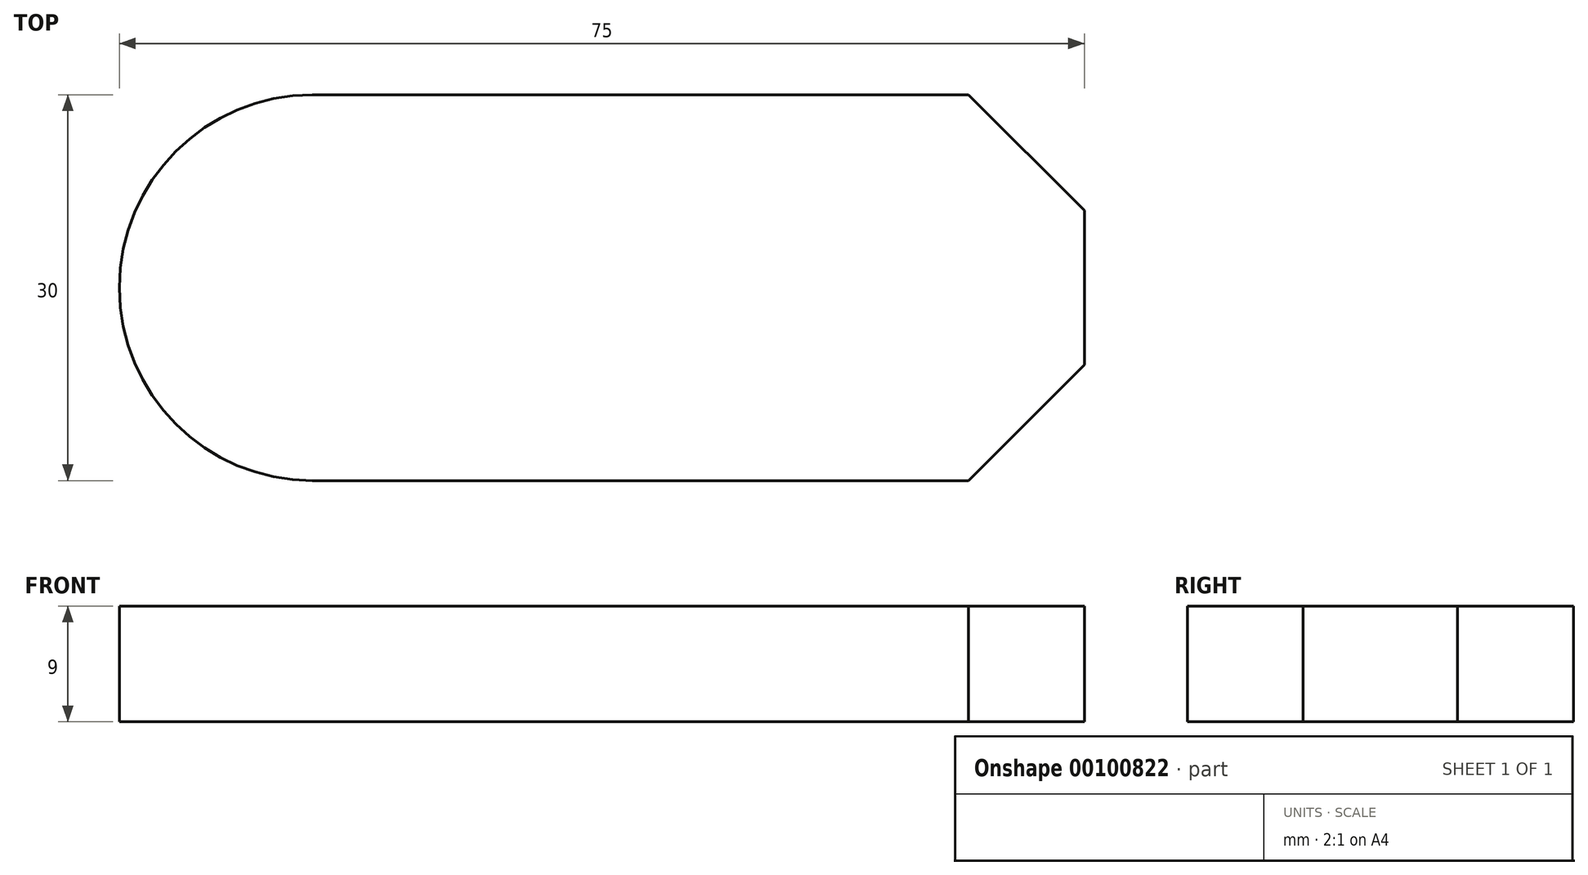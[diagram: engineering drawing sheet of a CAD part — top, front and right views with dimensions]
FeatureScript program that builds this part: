
annotation { "Feature Type Name" : "Feature", "Feature Type Description" : "" }
export const myFeature = defineFeature(function(context is Context, id is Id, definition is map)
    precondition{}
    {
        {
            var Q0;
            Q0=qCreatedBy(makeId("Top.planeOp"),FACE);
            var sketch = newSketch(context, id + "F0", { "sketchPlane" : qUnion([Q0])});
            skLineSegment(sketch, "E0.top", {"start": v(0, 30) * mm, "end": v(51, 30) * mm});
            skArc(sketch, "E1", {"start": v(0, 30) * mm, "mid": v(-15, 15) * mm, "end": v(0, 0) * mm});
            skPoint(sketch, "E2.end.orphan", {"position": v(42.52, 49.43) * mm});
            skPoint(sketch, "E3.end.orphan", {"position": v(42.52, 0) * mm});
            skPoint(sketch, "E4.start.orphan", {"position": v(42.52, 19.13) * mm});
            skLineSegment(sketch, "E5", {"start": v(51, 0) * mm, "end": v(0, 0) * mm});
            skLineSegment(sketch, "E6", {"start": v(60, 21) * mm, "end": v(60, 9) * mm});
            skLineSegment(sketch, "E7", {"start": v(51, 0) * mm, "end": v(60, 9) * mm});
            skLineSegment(sketch, "E8", {"start": v(51, 30) * mm, "end": v(60, 21) * mm});
            skPoint(sketch, "E9.orphan", {"position": v(60, 30) * mm});
            skPoint(sketch, "E10.start.orphan", {"position": v(60, 0) * mm});
            skSolve(sketch);
        }
        {
            var Q0;
            Q0 = qSketchRegion(id + "F0", true);
            extrude(context, id + "F1", {"entities" : qUnion([Q0]), "depth" : 9 * mm});
        }
    });
